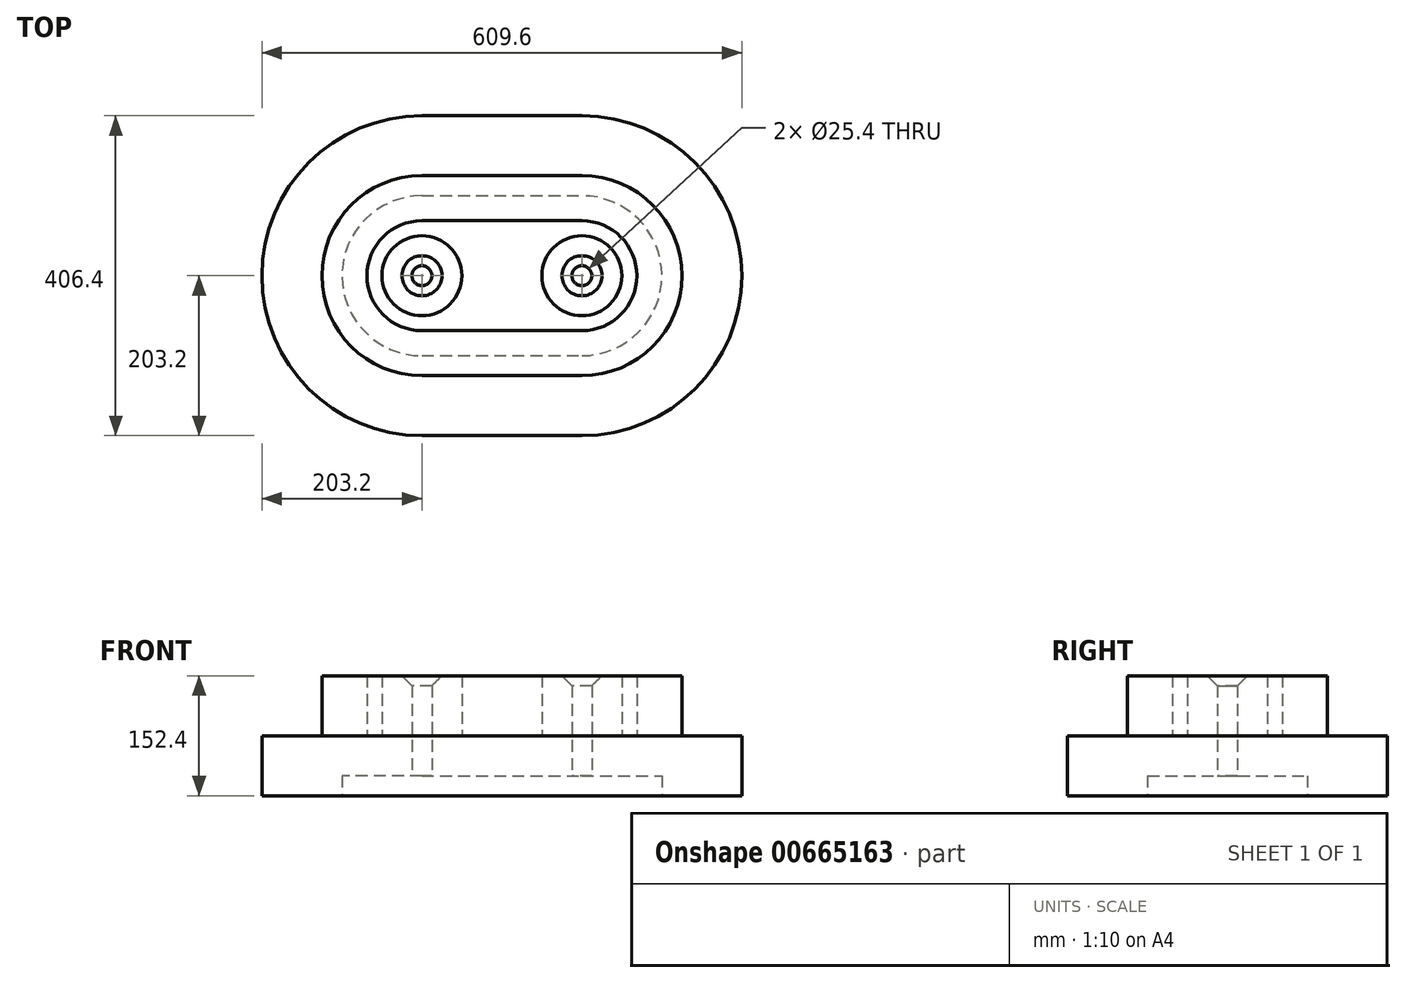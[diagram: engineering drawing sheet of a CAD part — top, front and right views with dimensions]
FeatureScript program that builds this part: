
annotation { "Feature Type Name" : "Feature", "Feature Type Description" : "" }
export const myFeature = defineFeature(function(context is Context, id is Id, definition is map)
    precondition{}
    {
        {
            var Q0;
            Q0=qCreatedBy(makeId("Top.planeOp"),FACE);
            var sketch = newSketch(context, id + "F0", { "sketchPlane" : qUnion([Q0])});
            skLineSegment(sketch, "E0", {"start": v(0, 0) * mm, "end": v(203.2, 0) * mm, "construction": true});
            skArc(sketch, "E1", {"start": v(0, 203.2) * mm, "mid": v(-203.2, 0) * mm, "end": v(0, -203.2) * mm});
            skLineSegment(sketch, "E2", {"start": v(0, 203.2) * mm, "end": v(203.2, 203.2) * mm});
            skLineSegment(sketch, "E3", {"start": v(203.2, -203.2) * mm, "end": v(0, -203.2) * mm});
            skArc(sketch, "E4.trimOffspring", {"start": v(203.2, -203.2) * mm, "mid": v(406.4, 0) * mm, "end": v(203.2, 203.2) * mm});
            skSolve(sketch);
        }
        {
            var Q0;
            Q0=makeQuery(id+"F0.imprint","IMPRINT",FACE,{"disambiguationData":[TD([[makeQuery(id+"F0.imprint","IMPRINT",EDGE,{"derivedFrom":sQuery(id+"F0.wireOp",EDGE,"E1")}),1.0]])]});
            extrude(context, id + "F1", {"entities" : qUnion([Q0]), "depth" : 76.2 * mm, "offsetDistance" : 25.4 * mm});
        }
        {
            var Q0;
            Q0=makeQuery(id+"F1.opExtrude","CAP_FACE",FACE,{"disambiguationData":[OSD([sQuery(id+"F0.wireOp",EDGE,"E1"),sQuery(id+"F0.wireOp",EDGE,"E2"),sQuery(id+"F0.wireOp",EDGE,"E3"),sQuery(id+"F0.wireOp",EDGE,"E4.trimOffspring")])],"isStart":false});
            var sketch = newSketch(context, id + "F2", { "sketchPlane" : qUnion([Q0])});
            skCircle(sketch, "E5", {"center": v(0, 0) * mm, "radius": 12.7 * mm});
            skCircle(sketch, "E6", {"center": v(203.2, 0) * mm, "radius": 25.4 * mm});
            skCircle(sketch, "E7", {"center": v(203.2, 0) * mm, "radius": 12.7 * mm});
            skCircle(sketch, "E8", {"center": v(0, 0) * mm, "radius": 25.4 * mm});
            skArc(sketch, "E9", {"start": v(203.2, -127) * mm, "mid": v(330.2, 0) * mm, "end": v(203.2, 127) * mm});
            skArc(sketch, "E10", {"start": v(0, 127) * mm, "mid": v(-127, 0) * mm, "end": v(0, -127) * mm});
            skArc(sketch, "E11", {"start": v(0, 69.85) * mm, "mid": v(-69.85, 0) * mm, "end": v(0, -69.85) * mm});
            skArc(sketch, "E12", {"start": v(203.2, -69.85) * mm, "mid": v(273.05, 0) * mm, "end": v(203.2, 69.85) * mm});
            skLineSegment(sketch, "E13", {"start": v(0, 127) * mm, "end": v(203.2, 127) * mm});
            skLineSegment(sketch, "E14", {"start": v(203.2, -127) * mm, "end": v(0, -127) * mm});
            skLineSegment(sketch, "E15", {"start": v(0, 69.85) * mm, "end": v(203.2, 69.85) * mm});
            skLineSegment(sketch, "E16", {"start": v(0, -69.85) * mm, "end": v(203.2, -69.85) * mm});
            skCircle(sketch, "E17", {"center": v(0, 0) * mm, "radius": 50.8 * mm});
            skCircle(sketch, "E18", {"center": v(203.2, 0) * mm, "radius": 50.8 * mm});
            skSolve(sketch);
        }
        {
            var Q0;
            Q0=makeQuery(id+"F2.imprint","IMPRINT",FACE,{"disambiguationData":[TD([[makeQuery(id+"F2.imprint","IMPRINT",EDGE,{"derivedFrom":sQuery(id+"F2.wireOp",EDGE,"E9")}),1.0]])]});
            var Q1;
            Q1=makeQuery(id+"F2.imprint","IMPRINT",FACE,{"disambiguationData":[TD([[makeQuery(id+"F2.imprint","IMPRINT",EDGE,{"derivedFrom":sQuery(id+"F2.wireOp",EDGE,"E8")}),-1.0]])]});
            var Q2;
            Q2=makeQuery(id+"F2.imprint","IMPRINT",FACE,{"disambiguationData":[TD([[makeQuery(id+"F2.imprint","IMPRINT",EDGE,{"derivedFrom":sQuery(id+"F2.wireOp",EDGE,"E6")}),-1.0]])]});
            var Q3;
            Q3=makeQuery(id+"F2.imprint","IMPRINT",FACE,{"disambiguationData":[TD([[makeQuery(id+"F2.imprint","IMPRINT",EDGE,{"derivedFrom":sQuery(id+"F2.wireOp",EDGE,"E5")}),-1.0]])]});
            var Q4;
            Q4=makeQuery(id+"F2.imprint","IMPRINT",FACE,{"disambiguationData":[TD([[makeQuery(id+"F2.imprint","IMPRINT",EDGE,{"derivedFrom":sQuery(id+"F2.wireOp",EDGE,"E6")}),1.0]])]});
            extrude(context, id + "F3", {"entities" : qUnion([Q0, Q1, Q2, Q3, Q4]), "operationType" : NewBodyOperationType.ADD, "depth" : 76.2 * mm, "offsetDistance" : 25.4 * mm});
        }
        {
            var Q0;
            Q0=makeQuery(id+"F3.opExtrude","CAP_EDGE",EDGE,{"disambiguationData":[OSD([sQuery(id+"F2.wireOp",EDGE,"E5")])],"isStart":false});
            var Q1;
            Q1=makeQuery(id+"F3.opExtrude","CAP_EDGE",EDGE,{"disambiguationData":[OSD([sQuery(id+"F2.wireOp",EDGE,"E7")])],"isStart":false});
            chamfer(context, id + "F4", {"entities" : qUnion([Q0, Q1]), "width" : 12.7 * mm, "tangentPropagation" : true});
        }
        {
            var Q0;
            Q0=makeQuery(id+"F1.opExtrude","CAP_FACE",FACE,{"disambiguationData":[OSD([sQuery(id+"F0.wireOp",EDGE,"E1"),sQuery(id+"F0.wireOp",EDGE,"E2"),sQuery(id+"F0.wireOp",EDGE,"E3"),sQuery(id+"F0.wireOp",EDGE,"E4.trimOffspring")])],"isStart":true});
            var sketch = newSketch(context, id + "F5", { "sketchPlane" : qUnion([Q0])});
            skArc(sketch, "E19", {"start": v(0, 101.6) * mm, "mid": v(-101.6, 0) * mm, "end": v(0, -101.6) * mm});
            skArc(sketch, "E20", {"start": v(203.2, -101.6) * mm, "mid": v(304.8, 0) * mm, "end": v(203.2, 101.6) * mm});
            skLineSegment(sketch, "E21", {"start": v(0, 101.6) * mm, "end": v(203.2, 101.6) * mm});
            skLineSegment(sketch, "E22", {"start": v(0, -101.6) * mm, "end": v(203.2, -101.6) * mm});
            skSolve(sketch);
        }
        {
            var Q0;
            Q0=makeQuery(id+"F5.imprint","IMPRINT",FACE,{"disambiguationData":[TD([[makeQuery(id+"F5.imprint","IMPRINT",EDGE,{"derivedFrom":sQuery(id+"F5.wireOp",EDGE,"E19")}),1.0]])]});
            extrude(context, id + "F6", {"entities" : qUnion([Q0]), "operationType" : NewBodyOperationType.REMOVE, "oppositeDirection" : true, "depth" : 25.4 * mm, "offsetDistance" : 25.4 * mm});
        }
        {
            var Q0;
            Q0=makeQuery(id+"F3.boolean.opBoolean","SPLIT",FACE,{"disambiguationData":[TD([makeQuery(id+"F3.opExtrude","SWEPT_FACE",FACE,{"disambiguationData":[OSD([sQuery(id+"F2.wireOp",EDGE,"E5")])]})])],"derivedFrom":makeQuery(id+"F1.opExtrude","CAP_FACE",FACE,{"disambiguationData":[OSD([sQuery(id+"F0.wireOp",EDGE,"E1"),sQuery(id+"F0.wireOp",EDGE,"E2"),sQuery(id+"F0.wireOp",EDGE,"E3"),sQuery(id+"F0.wireOp",EDGE,"E4.trimOffspring")])],"isStart":false})});
            var Q1;
            Q1=makeQuery(id+"F3.boolean.opBoolean","SPLIT",FACE,{"disambiguationData":[TD([makeQuery(id+"F3.opExtrude","SWEPT_FACE",FACE,{"disambiguationData":[OSD([sQuery(id+"F2.wireOp",EDGE,"E7")])]})])],"derivedFrom":makeQuery(id+"F1.opExtrude","CAP_FACE",FACE,{"disambiguationData":[OSD([sQuery(id+"F0.wireOp",EDGE,"E1"),sQuery(id+"F0.wireOp",EDGE,"E2"),sQuery(id+"F0.wireOp",EDGE,"E3"),sQuery(id+"F0.wireOp",EDGE,"E4.trimOffspring")])],"isStart":false})});
            extrude(context, id + "F7", {"entities" : qUnion([Q0, Q1]), "operationType" : NewBodyOperationType.REMOVE, "oppositeDirection" : true, "depth" : 50.8 * mm, "offsetDistance" : 25.4 * mm});
        }
    });
